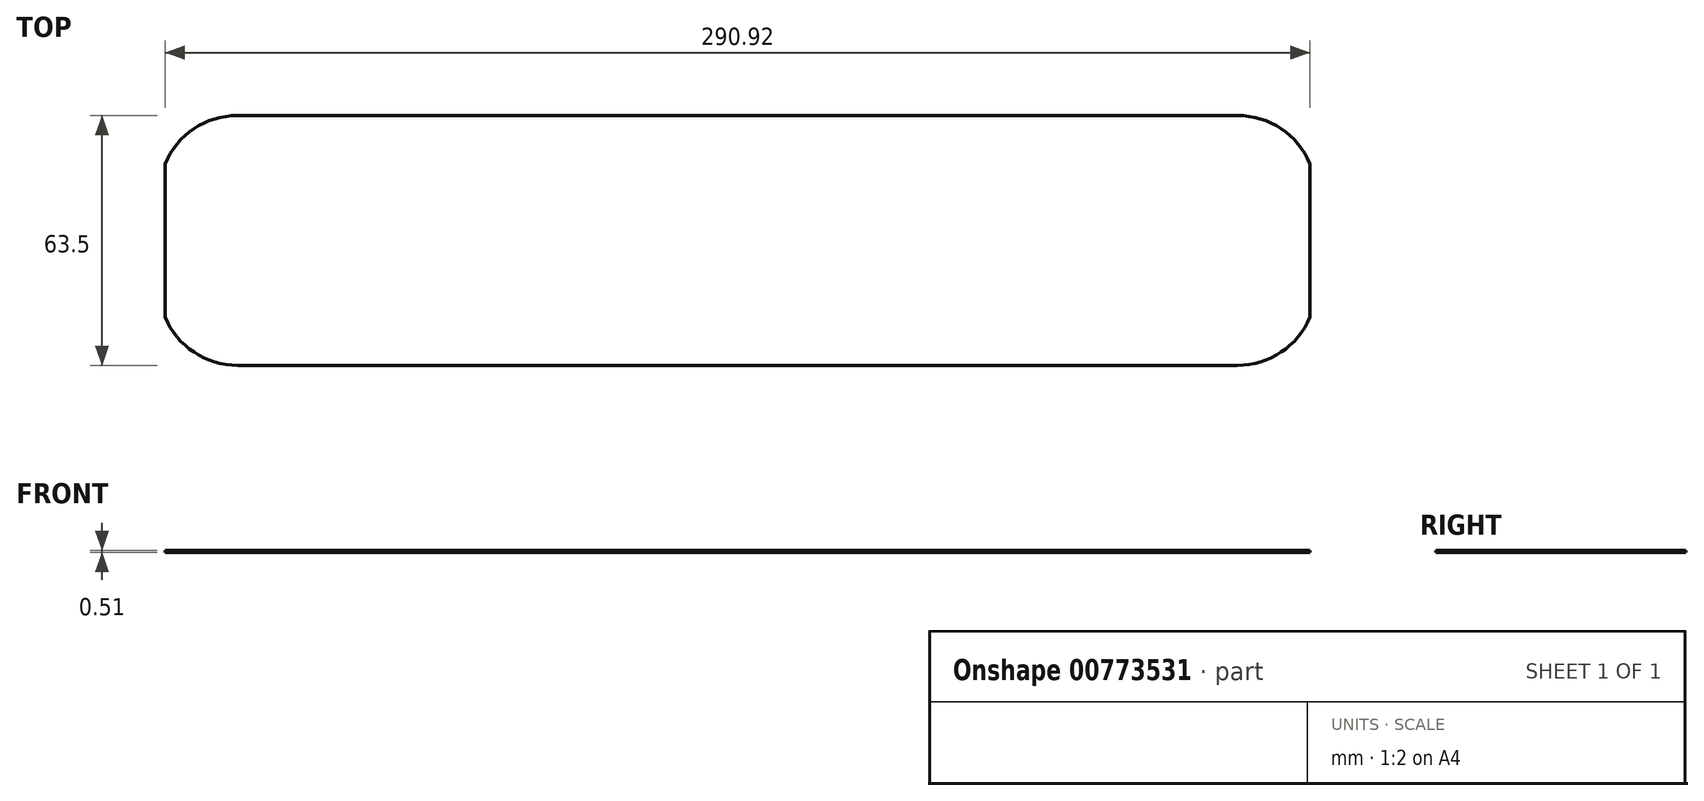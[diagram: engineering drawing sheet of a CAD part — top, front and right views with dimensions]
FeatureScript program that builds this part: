
annotation { "Feature Type Name" : "Feature", "Feature Type Description" : "" }
export const myFeature = defineFeature(function(context is Context, id is Id, definition is map)
    precondition{}
    {
        {
            var Q0;
            Q0=qCreatedBy(makeId("Top.planeOp"),FACE);
            var sketch = newSketch(context, id + "F0", { "sketchPlane" : qUnion([Q0])});
            skLineSegment(sketch, "E0.bottom", {"start": v(127, -31.75) * mm, "end": v(-127, -31.75) * mm});
            skLineSegment(sketch, "E0.top", {"start": v(127, 31.75) * mm, "end": v(-127, 31.75) * mm});
            skLineSegment(sketch, "E0.left", {"start": v(127, -31.75) * mm, "end": v(127, 31.75) * mm});
            skLineSegment(sketch, "E0.right", {"start": v(-127, -31.75) * mm, "end": v(-127, 31.75) * mm});
            skPoint(sketch, "E0.middle", {"position": v(0, 0) * mm});
            skPoint(sketch, "E1", {"position": v(145.46, 19.47) * mm});
            skPoint(sketch, "E2.MirrorP", {"position": v(145.46, -19.47) * mm});
            skPoint(sketch, "E3.MirrorP", {"position": v(-145.46, 19.47) * mm});
            skPoint(sketch, "E4.MirrorP", {"position": v(-145.46, -19.47) * mm});
            skLineSegment(sketch, "E5", {"start": v(-145.46, 19.47) * mm, "end": v(-145.46, -19.47) * mm});
            skLineSegment(sketch, "E6.MirrorCS", {"start": v(145.46, 19.47) * mm, "end": v(145.46, -19.47) * mm});
            skArc(sketch, "E7", {"start": v(-127, 31.75) * mm, "mid": v(-138.09, 28.4) * mm, "end": v(-145.46, 19.47) * mm});
            skArc(sketch, "E8.MirrorCS", {"start": v(-127, -31.75) * mm, "mid": v(-138.09, -28.4) * mm, "end": v(-145.46, -19.47) * mm});
            skArc(sketch, "E9.MirrorCS", {"start": v(127, 31.75) * mm, "mid": v(138.09, 28.4) * mm, "end": v(145.46, 19.47) * mm});
            skArc(sketch, "E10.MirrorCS", {"start": v(127, -31.75) * mm, "mid": v(138.09, -28.4) * mm, "end": v(145.46, -19.47) * mm});
            skSolve(sketch);
        }
        {
            var Q0;
            Q0 = qSketchRegion(id + "F0", true);
            extrude(context, id + "F1", {"entities" : qUnion([Q0]), "depth" : 0.5 * mm, "offsetDistance" : 25.4 * mm});
        }
    });
